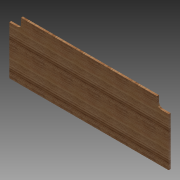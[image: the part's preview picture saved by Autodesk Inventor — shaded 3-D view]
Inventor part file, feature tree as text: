
AUTODESK INVENTOR PART (.ipt)
format: ipt  version: 2012 (Build 160160000, 160)  size: 102,912 bytes
history: native  units: in
note: dims shown in document units (in); Inventor stores cm internally (conversion verified against a paired STEP export)
features: extrude x1, sketch x1
ambient origin geometry x8: Origin, YZ Plane, XZ Plane, XY Plane, X Axis, Y Axis, Z Axis, Center Point
bodies: Solid1 (feature_tree)
feature tree (2):
  extrude  "Extrusion1"  Depth=20.5in
  sketch  "Sketch1"  dims[d0=7.5in d1=20.5in d2=0.25in d3=0.0in d4=1.0in d5=1.0in d6=1.0in d7=0.75in d8=1.0in d9=0.75in]
